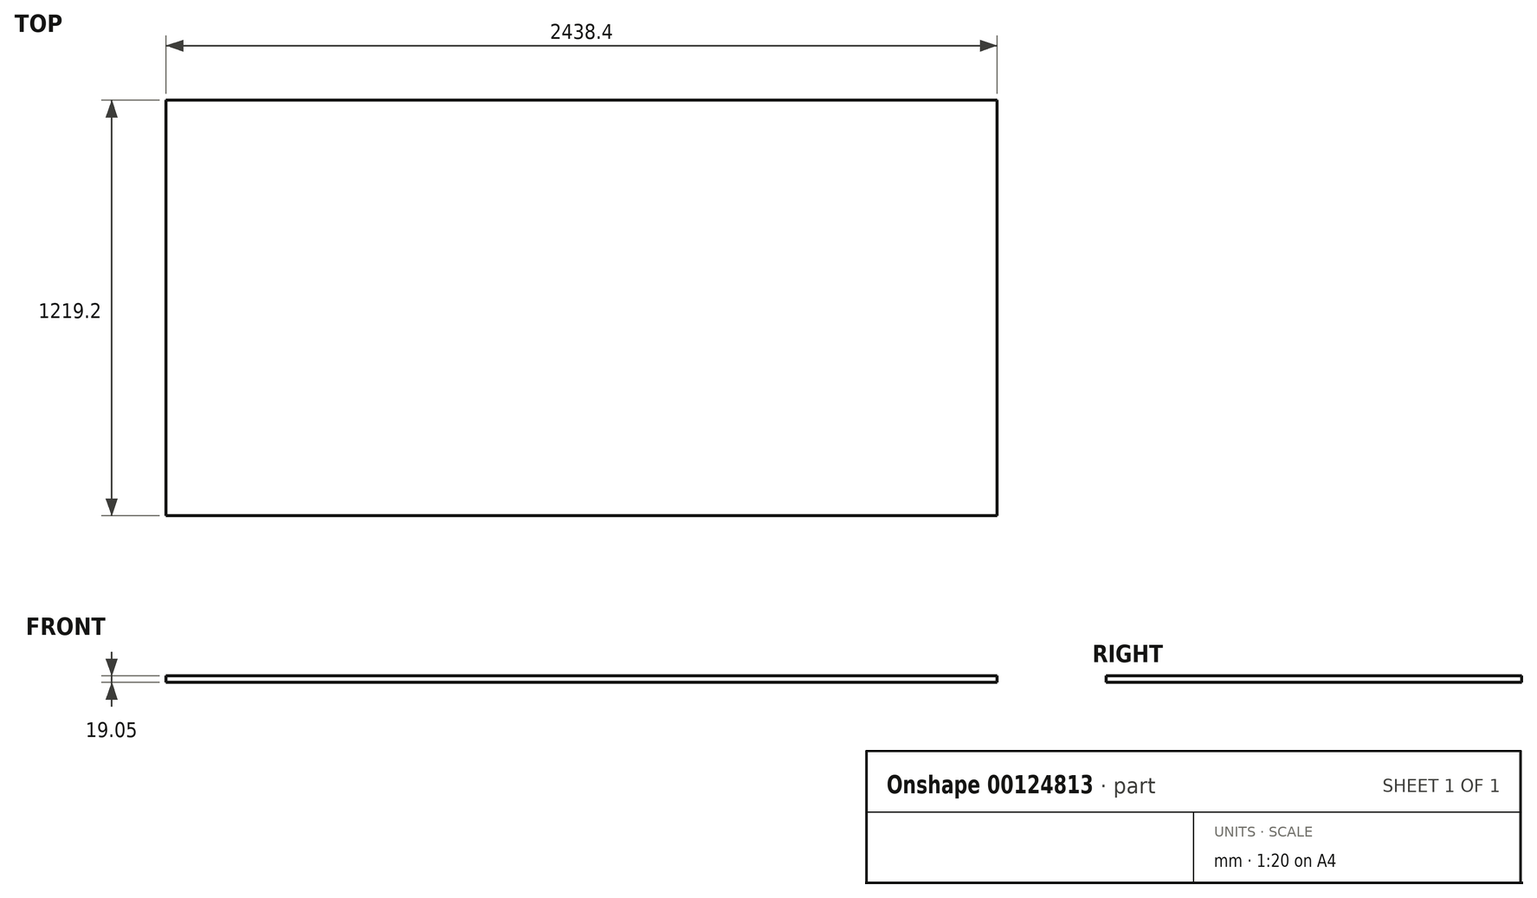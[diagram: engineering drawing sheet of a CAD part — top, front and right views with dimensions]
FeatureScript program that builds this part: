
annotation { "Feature Type Name" : "Feature", "Feature Type Description" : "" }
export const myFeature = defineFeature(function(context is Context, id is Id, definition is map)
    precondition{}
    {
        {
            var Q0;
            Q0=qCreatedBy(makeId("Top.planeOp"),FACE);
            var sketch = newSketch(context, id + "F0", { "sketchPlane" : qUnion([Q0])});
            skLineSegment(sketch, "E0.bottom", {"start": v(-1219.2, 609.6) * mm, "end": v(1219.2, 609.6) * mm});
            skLineSegment(sketch, "E0.top", {"start": v(-1219.2, -609.6) * mm, "end": v(1219.2, -609.6) * mm});
            skLineSegment(sketch, "E0.left", {"start": v(-1219.2, 609.6) * mm, "end": v(-1219.2, -609.6) * mm});
            skLineSegment(sketch, "E0.right", {"start": v(1219.2, 609.6) * mm, "end": v(1219.2, -609.6) * mm});
            skSolve(sketch);
        }
        {
            var Q0;
            Q0=makeQuery(id+"F0.imprint","IMPRINT",FACE,{"disambiguationData":[TD([[makeQuery(id+"F0.imprint","IMPRINT",EDGE,{"derivedFrom":sQuery(id+"F0.wireOp",EDGE,"E0.bottom")}),-1.0]])]});
            extrude(context, id + "F1", {"entities" : qUnion([Q0]), "depth" : 19.05 * mm});
        }
    });
